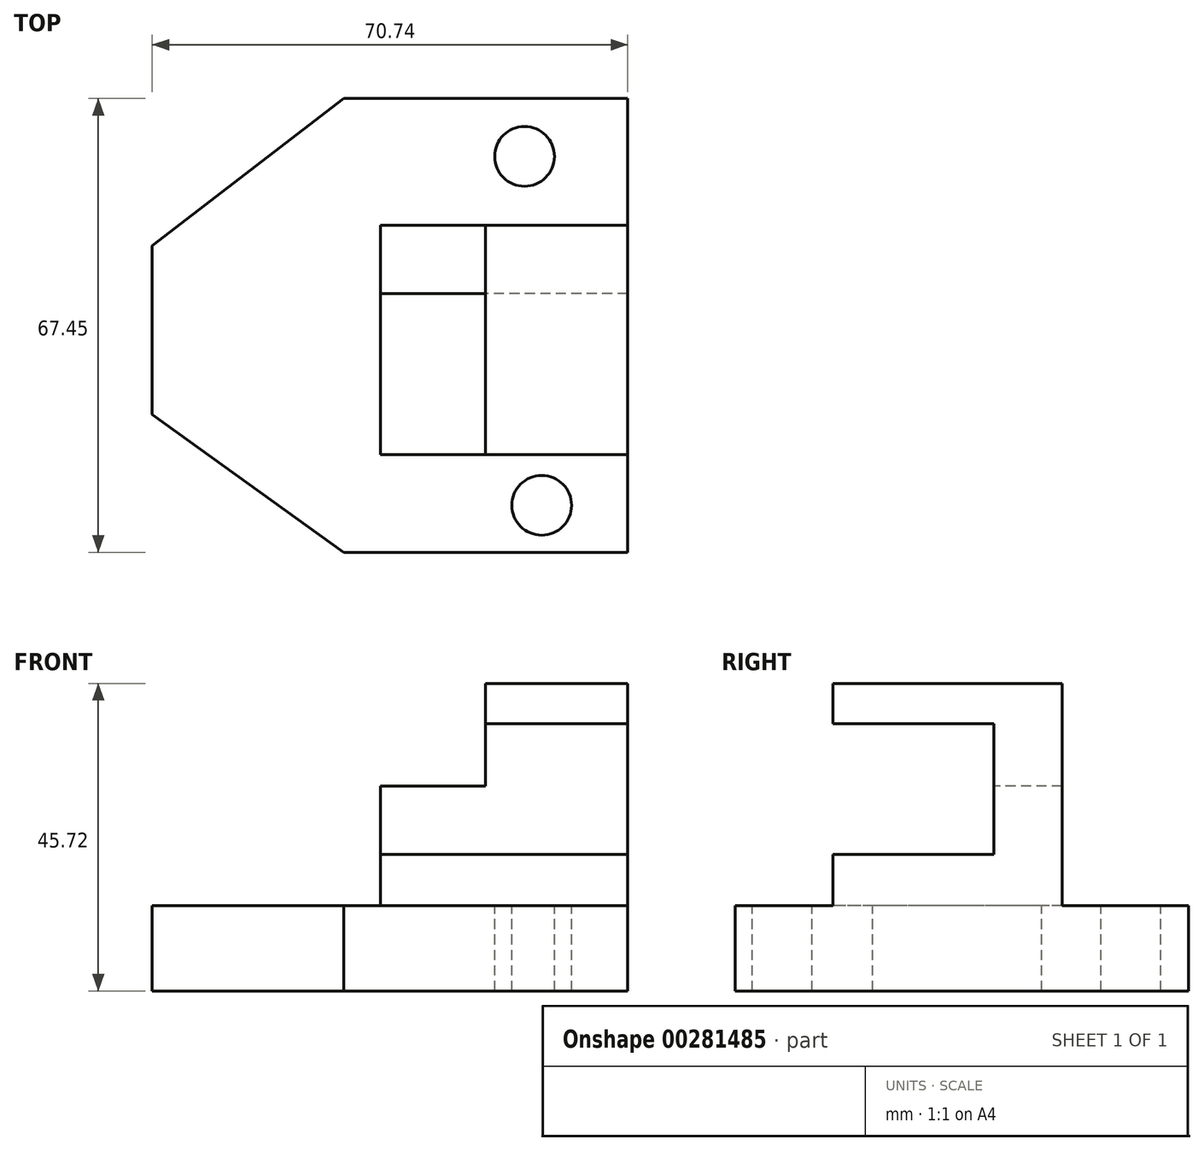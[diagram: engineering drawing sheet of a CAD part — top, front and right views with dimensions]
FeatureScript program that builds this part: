
annotation { "Feature Type Name" : "Feature", "Feature Type Description" : "" }
export const myFeature = defineFeature(function(context is Context, id is Id, definition is map)
    precondition{}
    {
        {
            var Q0;
            Q0=qCreatedBy(makeId("Top.planeOp"),FACE);
            var sketch = newSketch(context, id + "F0", { "sketchPlane" : qUnion([Q0])});
            skLineSegment(sketch, "E0.bottom", {"start": v(-49.2, 18.84) * mm, "end": v(42.21, 18.84) * mm});
            skLineSegment(sketch, "E0.top", {"start": v(-49.2, -48.61) * mm, "end": v(42.21, -48.61) * mm});
            skLineSegment(sketch, "E0.left", {"start": v(-49.2, 18.84) * mm, "end": v(-49.2, -48.61) * mm});
            skLineSegment(sketch, "E0.right", {"start": v(42.21, 18.84) * mm, "end": v(42.21, -48.61) * mm});
            skSolve(sketch);
        }
        {
            var Q0;
            Q0=makeQuery(id+"F0.imprint","IMPRINT",FACE,{"disambiguationData":[TD([[makeQuery(id+"F0.imprint","IMPRINT",EDGE,{"derivedFrom":sQuery(id+"F0.wireOp",EDGE,"E0.bottom")}),-1.0]])]});
            extrude(context, id + "F1", {"entities" : qUnion([Q0]), "depth" : 12.7 * mm});
        }
        {
            var Q0;
            Q0=makeQuery(id+"F1.opExtrude","CAP_FACE",FACE,{"disambiguationData":[OSD([sQuery(id+"F0.wireOp",EDGE,"E0.bottom"),sQuery(id+"F0.wireOp",EDGE,"E0.top"),sQuery(id+"F0.wireOp",EDGE,"E0.left"),sQuery(id+"F0.wireOp",EDGE,"E0.right")])],"isStart":false});
            var sketch = newSketch(context, id + "F2", { "sketchPlane" : qUnion([Q0])});
            skLineSegment(sketch, "E1", {"start": v(-49.2, -23.03) * mm, "end": v(-15.7, -48.61) * mm});
            skLineSegment(sketch, "E2", {"start": v(-49.2, 0) * mm, "end": v(-15.7, 18.84) * mm});
            skSolve(sketch);
        }
        {
            var Q0;
            {var subQ0=sQuery(id+"F2.wireOp",EDGE,"E2");Q0=makeQuery(id+"F2.imprint","IMPRINT",FACE,{"disambiguationData":[TD([[makeQuery(id+"F2.imprint","IMPRINT",EDGE,{"derivedFrom":subQ0}),1.0]])]});}
            var Q1;
            {var subQ0=sQuery(id+"F2.wireOp",EDGE,"E1");Q1=makeQuery(id+"F2.imprint","IMPRINT",FACE,{"disambiguationData":[TD([[makeQuery(id+"F2.imprint","IMPRINT",EDGE,{"derivedFrom":subQ0}),-1.0]])]});}
            extrude(context, id + "F3", {"entities" : qUnion([Q0, Q1]), "operationType" : NewBodyOperationType.REMOVE, "oppositeDirection" : true, "depth" : 25.4 * mm});
        }
        {
            var Q0;
            Q0=makeQuery(id+"F1.opExtrude","CAP_FACE",FACE,{"disambiguationData":[OSD([sQuery(id+"F0.wireOp",EDGE,"E0.bottom"),sQuery(id+"F0.wireOp",EDGE,"E0.top"),sQuery(id+"F0.wireOp",EDGE,"E0.left"),sQuery(id+"F0.wireOp",EDGE,"E0.right")])],"isStart":false});
            var sketch = newSketch(context, id + "F4", { "sketchPlane" : qUnion([Q0])});
            skLineSegment(sketch, "E3.bottom", {"start": v(-9.19, 0) * mm, "end": v(42.21, 0) * mm});
            skLineSegment(sketch, "E3.top", {"start": v(-9.19, -34.08) * mm, "end": v(42.21, -34.08) * mm});
            skLineSegment(sketch, "E3.left", {"start": v(-9.19, 0) * mm, "end": v(-9.19, -34.08) * mm});
            skLineSegment(sketch, "E3.right", {"start": v(42.21, 0) * mm, "end": v(42.21, -34.08) * mm});
            skSolve(sketch);
        }
        {
            var Q0;
            Q0=makeQuery(id+"F4.imprint","IMPRINT",FACE,{"disambiguationData":[TD([[makeQuery(id+"F4.imprint","IMPRINT",EDGE,{"derivedFrom":sQuery(id+"F4.wireOp",EDGE,"E3.bottom")}),-1.0]])]});
            extrude(context, id + "F5", {"entities" : qUnion([Q0]), "operationType" : NewBodyOperationType.ADD, "depth" : 7.62 * mm});
        }
        {
            var Q0;
            Q0=makeQuery(id+"F5.opExtrude","CAP_FACE",FACE,{"disambiguationData":[OSD([sQuery(id+"F4.wireOp",EDGE,"E3.bottom"),sQuery(id+"F4.wireOp",EDGE,"E3.top"),sQuery(id+"F4.wireOp",EDGE,"E3.left"),sQuery(id+"F4.wireOp",EDGE,"E3.right")])],"isStart":false});
            var sketch = newSketch(context, id + "F6", { "sketchPlane" : qUnion([Q0])});
            skLineSegment(sketch, "E4.bottom", {"start": v(42.21, 0) * mm, "end": v(21.05, 0) * mm});
            skLineSegment(sketch, "E4.top", {"start": v(42.21, -34.08) * mm, "end": v(21.05, -34.08) * mm});
            skLineSegment(sketch, "E4.left", {"start": v(42.21, 0) * mm, "end": v(42.21, -34.08) * mm});
            skLineSegment(sketch, "E4.right", {"start": v(21.05, 0) * mm, "end": v(21.05, -34.08) * mm});
            skSolve(sketch);
        }
        {
            var Q0;
            Q0=makeQuery(id+"F6.imprint","IMPRINT",FACE,{"disambiguationData":[TD([[makeQuery(id+"F6.imprint","IMPRINT",EDGE,{"derivedFrom":sQuery(id+"F6.wireOp",EDGE,"E4.bottom")}),-1.0]])]});
            extrude(context, id + "F7", {"entities" : qUnion([Q0]), "operationType" : NewBodyOperationType.ADD, "depth" : 25.4 * mm});
        }
        {
            var Q0;
            Q0=makeQuery(id+"F7.opExtrude","SWEPT_FACE",FACE,{"disambiguationData":[OSD([sQuery(id+"F6.wireOp",EDGE,"E4.right")])]});
            var sketch = newSketch(context, id + "F8", { "sketchPlane" : qUnion([Q0])});
            skLineSegment(sketch, "E5.bottom", {"start": v(10.16, 20.32) * mm, "end": v(34.08, 20.32) * mm});
            skLineSegment(sketch, "E5.top", {"start": v(10.16, 39.74) * mm, "end": v(34.08, 39.74) * mm});
            skLineSegment(sketch, "E5.left", {"start": v(10.16, 20.32) * mm, "end": v(10.16, 39.74) * mm});
            skLineSegment(sketch, "E5.right", {"start": v(34.08, 20.32) * mm, "end": v(34.08, 39.74) * mm});
            skSolve(sketch);
        }
        {
            var Q0;
            Q0=makeQuery(id+"F8.imprint","IMPRINT",FACE,{"disambiguationData":[TD([[makeQuery(id+"F8.imprint","IMPRINT",EDGE,{"derivedFrom":sQuery(id+"F8.wireOp",EDGE,"E5.bottom")}),1.0]])]});
            extrude(context, id + "F9", {"entities" : qUnion([Q0]), "operationType" : NewBodyOperationType.REMOVE, "oppositeDirection" : true, "depth" : 25.4 * mm});
        }
        {
            var Q0;
            Q0=makeQuery(id+"F9.boolean.opBoolean","MERGE",FACE,{"derivedFrom":[makeQuery(id+"F5.opExtrude","CAP_FACE",FACE,{"disambiguationData":[OSD([sQuery(id+"F4.wireOp",EDGE,"E3.bottom"),sQuery(id+"F4.wireOp",EDGE,"E3.top"),sQuery(id+"F4.wireOp",EDGE,"E3.left"),sQuery(id+"F4.wireOp",EDGE,"E3.right")])],"isStart":false}),makeQuery(id+"F9.opExtrude","SWEPT_FACE",FACE,{"disambiguationData":[OSD([sQuery(id+"F8.wireOp",EDGE,"E5.bottom")])]})]});
            var sketch = newSketch(context, id + "F10", { "sketchPlane" : qUnion([Q0])});
            skLineSegment(sketch, "E6.bottom", {"start": v(-9.19, 0) * mm, "end": v(5.47, 0) * mm});
            skLineSegment(sketch, "E6.top", {"start": v(-9.19, -34.08) * mm, "end": v(5.47, -34.08) * mm});
            skLineSegment(sketch, "E6.left", {"start": v(-9.19, 0) * mm, "end": v(-9.19, -34.08) * mm});
            skLineSegment(sketch, "E6.right", {"start": v(5.47, 0) * mm, "end": v(5.47, -34.08) * mm});
            skSolve(sketch);
        }
        {
            var Q0;
            Q0=makeQuery(id+"F10.imprint","IMPRINT",FACE,{"disambiguationData":[TD([[makeQuery(id+"F10.imprint","IMPRINT",EDGE,{"derivedFrom":sQuery(id+"F10.wireOp",EDGE,"E6.bottom")}),-1.0]])]});
            extrude(context, id + "F11", {"entities" : qUnion([Q0]), "operationType" : NewBodyOperationType.REMOVE, "oppositeDirection" : true, "depth" : 7.62 * mm});
        }
        {
            var Q0;
            Q0=makeQuery(id+"F9.boolean.opBoolean","MERGE",FACE,{"derivedFrom":[makeQuery(id+"F5.opExtrude","CAP_FACE",FACE,{"disambiguationData":[OSD([sQuery(id+"F4.wireOp",EDGE,"E3.bottom"),sQuery(id+"F4.wireOp",EDGE,"E3.top"),sQuery(id+"F4.wireOp",EDGE,"E3.left"),sQuery(id+"F4.wireOp",EDGE,"E3.right")])],"isStart":false}),makeQuery(id+"F9.opExtrude","SWEPT_FACE",FACE,{"disambiguationData":[OSD([sQuery(id+"F8.wireOp",EDGE,"E5.bottom")])]})]});
            var sketch = newSketch(context, id + "F12", { "sketchPlane" : qUnion([Q0])});
            skPoint(sketch, "E7.oppositeSnap0", {"position": v(21.05, -5.08) * mm});
            skLineSegment(sketch, "E7.bottom", {"start": v(5.47, 0) * mm, "end": v(21.05, 0) * mm});
            skLineSegment(sketch, "E7.top", {"start": v(5.47, -13.41) * mm, "end": v(21.05, -13.41) * mm});
            skLineSegment(sketch, "E7.left", {"start": v(5.47, 0) * mm, "end": v(5.47, -13.41) * mm});
            skLineSegment(sketch, "E7.right", {"start": v(21.05, 0) * mm, "end": v(21.05, -13.41) * mm});
            skSolve(sketch);
        }
        {
            var Q0;
            {var subQ1=sQuery(id+"F12.wireOp",EDGE,"E7.bottom");Q0=makeQuery(id+"F12.imprint","IMPRINT",FACE,{"disambiguationData":[TD([[makeQuery(id+"F12.imprint","IMPRINT",EDGE,{"derivedFrom":subQ1}),-1.0]])]});}
            extrude(context, id + "F13", {"entities" : qUnion([Q0]), "operationType" : NewBodyOperationType.ADD, "depth" : 10.16 * mm});
        }
        {
            var Q0;
            Q0=makeQuery(id+"F11.boolean.opBoolean","MERGE",FACE,{"derivedFrom":[makeQuery(id+"F1.opExtrude","CAP_FACE",FACE,{"disambiguationData":[OSD([sQuery(id+"F0.wireOp",EDGE,"E0.bottom"),sQuery(id+"F0.wireOp",EDGE,"E0.top"),sQuery(id+"F0.wireOp",EDGE,"E0.left"),sQuery(id+"F0.wireOp",EDGE,"E0.right")])],"isStart":false}),makeQuery(id+"F11.opExtrude","CAP_FACE",FACE,{"disambiguationData":[OSD([sQuery(id+"F10.wireOp",EDGE,"E6.bottom"),sQuery(id+"F10.wireOp",EDGE,"E6.top"),sQuery(id+"F10.wireOp",EDGE,"E6.left"),sQuery(id+"F10.wireOp",EDGE,"E6.right")])],"isStart":false})]});
            var sketch = newSketch(context, id + "F14", { "sketchPlane" : qUnion([Q0])});
            skLineSegment(sketch, "E8.bottom", {"start": v(-53.38, 19.3) * mm, "end": v(-28.53, 19.3) * mm});
            skLineSegment(sketch, "E8.top", {"start": v(-53.38, -38.81) * mm, "end": v(-28.53, -38.81) * mm});
            skLineSegment(sketch, "E8.left", {"start": v(-53.38, 19.3) * mm, "end": v(-53.38, -38.81) * mm});
            skLineSegment(sketch, "E8.right", {"start": v(-28.53, 19.3) * mm, "end": v(-28.53, -38.81) * mm});
            skSolve(sketch);
        }
        {
            var Q0;
            {var subQ5=makeQuery(id+"F1.opExtrude","CAP_EDGE",EDGE,{"disambiguationData":[OSD([sQuery(id+"F0.wireOp",EDGE,"E0.left")])],"isStart":false});Q0=makeQuery(id+"F14.imprint","IMPRINT",FACE,{"disambiguationData":[TD([[makeQuery(id+"F14.imprint","IMPRINT",EDGE,{"derivedFrom":subQ5}),1.0]])]});}
            extrude(context, id + "F15", {"entities" : qUnion([Q0]), "operationType" : NewBodyOperationType.REMOVE, "oppositeDirection" : true, "depth" : 25.4 * mm});
        }
        {
            var Q0;
            Q0=makeQuery(id+"F11.boolean.opBoolean","MERGE",FACE,{"derivedFrom":[makeQuery(id+"F1.opExtrude","CAP_FACE",FACE,{"disambiguationData":[OSD([sQuery(id+"F0.wireOp",EDGE,"E0.bottom"),sQuery(id+"F0.wireOp",EDGE,"E0.top"),sQuery(id+"F0.wireOp",EDGE,"E0.left"),sQuery(id+"F0.wireOp",EDGE,"E0.right")])],"isStart":false}),makeQuery(id+"F11.opExtrude","CAP_FACE",FACE,{"disambiguationData":[OSD([sQuery(id+"F10.wireOp",EDGE,"E6.bottom"),sQuery(id+"F10.wireOp",EDGE,"E6.top"),sQuery(id+"F10.wireOp",EDGE,"E6.left"),sQuery(id+"F10.wireOp",EDGE,"E6.right")])],"isStart":false})]});
            var sketch = newSketch(context, id + "F16", { "sketchPlane" : qUnion([Q0])});
            skLineSegment(sketch, "E9", {"start": v(-28.53, -28.14) * mm, "end": v(0, -48.61) * mm});
            skLineSegment(sketch, "E10", {"start": v(0, 18.84) * mm, "end": v(-28.53, -3.02) * mm});
            skSolve(sketch);
        }
        {
            var Q0;
            {var subQ0=sQuery(id+"F16.wireOp",EDGE,"E10");Q0=makeQuery(id+"F16.imprint","IMPRINT",FACE,{"disambiguationData":[TD([[makeQuery(id+"F16.imprint","IMPRINT",EDGE,{"derivedFrom":subQ0}),-1.0]])]});}
            var Q1;
            {var subQ0=sQuery(id+"F16.wireOp",EDGE,"E9");Q1=makeQuery(id+"F16.imprint","IMPRINT",FACE,{"disambiguationData":[TD([[makeQuery(id+"F16.imprint","IMPRINT",EDGE,{"derivedFrom":subQ0}),-1.0]])]});}
            extrude(context, id + "F17", {"entities" : qUnion([Q0, Q1]), "operationType" : NewBodyOperationType.REMOVE, "oppositeDirection" : true, "depth" : 25.4 * mm});
        }
        {
            var Q0;
            Q0=makeQuery(id+"F13.opExtrude","CAP_FACE",FACE,{"disambiguationData":[OSD([sQuery(id+"F12.wireOp",EDGE,"E7.bottom"),sQuery(id+"F12.wireOp",EDGE,"E7.top"),sQuery(id+"F12.wireOp",EDGE,"E7.left"),sQuery(id+"F12.wireOp",EDGE,"E7.right")])],"isStart":false});
            extrude(context, id + "F18", {"entities" : qUnion([Q0]), "operationType" : NewBodyOperationType.REMOVE, "oppositeDirection" : true, "depth" : 10.16 * mm});
        }
        {
            var Q0;
            Q0=makeQuery(id+"F18.boolean.opBoolean","MERGE",FACE,{"derivedFrom":[makeQuery(id+"F9.boolean.opBoolean","MERGE",FACE,{"derivedFrom":[makeQuery(id+"F5.opExtrude","CAP_FACE",FACE,{"disambiguationData":[OSD([sQuery(id+"F4.wireOp",EDGE,"E3.bottom"),sQuery(id+"F4.wireOp",EDGE,"E3.top"),sQuery(id+"F4.wireOp",EDGE,"E3.left"),sQuery(id+"F4.wireOp",EDGE,"E3.right")])],"isStart":false}),makeQuery(id+"F9.opExtrude","SWEPT_FACE",FACE,{"disambiguationData":[OSD([sQuery(id+"F8.wireOp",EDGE,"E5.bottom")])]})]}),makeQuery(id+"F18.opExtrude","CAP_FACE",FACE,{"disambiguationData":[OSD([sQuery(id+"F12.wireOp",EDGE,"E7.bottom"),sQuery(id+"F12.wireOp",EDGE,"E7.top"),sQuery(id+"F12.wireOp",EDGE,"E7.left"),sQuery(id+"F12.wireOp",EDGE,"E7.right")])],"isStart":false})]});
            var sketch = newSketch(context, id + "F19", { "sketchPlane" : qUnion([Q0])});
            skLineSegment(sketch, "E11.bottom", {"start": v(5.47, 0) * mm, "end": v(21.05, 0) * mm});
            skLineSegment(sketch, "E11.top", {"start": v(5.47, -10.16) * mm, "end": v(21.05, -10.16) * mm});
            skLineSegment(sketch, "E11.left", {"start": v(5.47, 0) * mm, "end": v(5.47, -10.16) * mm});
            skLineSegment(sketch, "E11.right", {"start": v(21.05, 0) * mm, "end": v(21.05, -10.16) * mm});
            skSolve(sketch);
        }
        {
            var Q0;
            Q0=makeQuery(id+"F19.imprint","IMPRINT",FACE,{"disambiguationData":[TD([[makeQuery(id+"F19.imprint","IMPRINT",EDGE,{"derivedFrom":sQuery(id+"F19.wireOp",EDGE,"E11.bottom")}),-1.0]])]});
            extrude(context, id + "F20", {"entities" : qUnion([Q0]), "operationType" : NewBodyOperationType.ADD, "depth" : 10.16 * mm});
        }
        {
            var Q0;
            Q0=makeQuery(id+"F11.boolean.opBoolean","MERGE",FACE,{"derivedFrom":[makeQuery(id+"F1.opExtrude","CAP_FACE",FACE,{"disambiguationData":[OSD([sQuery(id+"F0.wireOp",EDGE,"E0.bottom"),sQuery(id+"F0.wireOp",EDGE,"E0.top"),sQuery(id+"F0.wireOp",EDGE,"E0.left"),sQuery(id+"F0.wireOp",EDGE,"E0.right")])],"isStart":false}),makeQuery(id+"F11.opExtrude","CAP_FACE",FACE,{"disambiguationData":[OSD([sQuery(id+"F10.wireOp",EDGE,"E6.bottom"),sQuery(id+"F10.wireOp",EDGE,"E6.top"),sQuery(id+"F10.wireOp",EDGE,"E6.left"),sQuery(id+"F10.wireOp",EDGE,"E6.right")])],"isStart":false})]});
            var sketch = newSketch(context, id + "F21", { "sketchPlane" : qUnion([Q0])});
            skCircle(sketch, "E12", {"center": v(29.42, -41.4) * mm, "radius": 4.79 * mm});
            skCircle(sketch, "E13", {"center": v(26.4, 10) * mm, "radius": 4.98 * mm});
            skSolve(sketch);
        }
        {
            var Q0;
            Q0=makeQuery(id+"F21.imprint","IMPRINT",FACE,{"disambiguationData":[TD([[makeQuery(id+"F21.imprint","IMPRINT",EDGE,{"derivedFrom":sQuery(id+"F21.wireOp",EDGE,"E12")}),-1.0]])]});
            var sketch = newSketch(context, id + "F22", { "sketchPlane" : qUnion([Q0])});
            skLineSegment(sketch, "E14", {"start": v(26.86, 10.23) * mm, "end": v(46.87, 10.23) * mm});
            skLineSegment(sketch, "E15", {"start": v(26.86, 10.23) * mm, "end": v(24.54, 24.19) * mm});
            skLineSegment(sketch, "E16", {"start": v(26.86, 10.23) * mm, "end": v(13.84, 10.23) * mm});
            skLineSegment(sketch, "E17", {"start": v(26.86, 10.23) * mm, "end": v(28.57, 0) * mm});
            skLineSegment(sketch, "E18", {"start": v(29.42, -41.63) * mm, "end": v(40.82, -41.63) * mm});
            skLineSegment(sketch, "E19", {"start": v(29.42, -41.63) * mm, "end": v(27.57, -30.5) * mm});
            skLineSegment(sketch, "E20", {"start": v(29.42, -41.63) * mm, "end": v(18.96, -41.63) * mm});
            skLineSegment(sketch, "E21", {"start": v(29.42, -41.63) * mm, "end": v(29.42, -51.4) * mm});
            skSolve(sketch);
        }
        {
            var Q0;
            Q0=sQuery(id+"F22.wireOp",VERTEX,"E17.start");
            var Q1;
            Q1=sQuery(id+"F22.wireOp",VERTEX,"E20.start");
            var Q2;
            Q2=makeQuery(id+"F1.opExtrude","SWEPT_BODY",BODY,{"disambiguationData":[OSD([sQuery(id+"F0.wireOp",EDGE,"E0.bottom"),sQuery(id+"F0.wireOp",EDGE,"E0.top"),sQuery(id+"F0.wireOp",EDGE,"E0.left"),sQuery(id+"F0.wireOp",EDGE,"E0.right")])]});
            hole(context, id + "F23", {"style" : HoleStyle.SIMPLE, "endStyle" : HoleEndStyle.THROUGH, "holeDiameter" : 8.9 * mm, "tappedDepth" : 12.7 * mm, "tapClearance" : 3, "locations" : qUnion([Q0, Q1]), "scope" : qUnion([Q2])});
        }
    });
